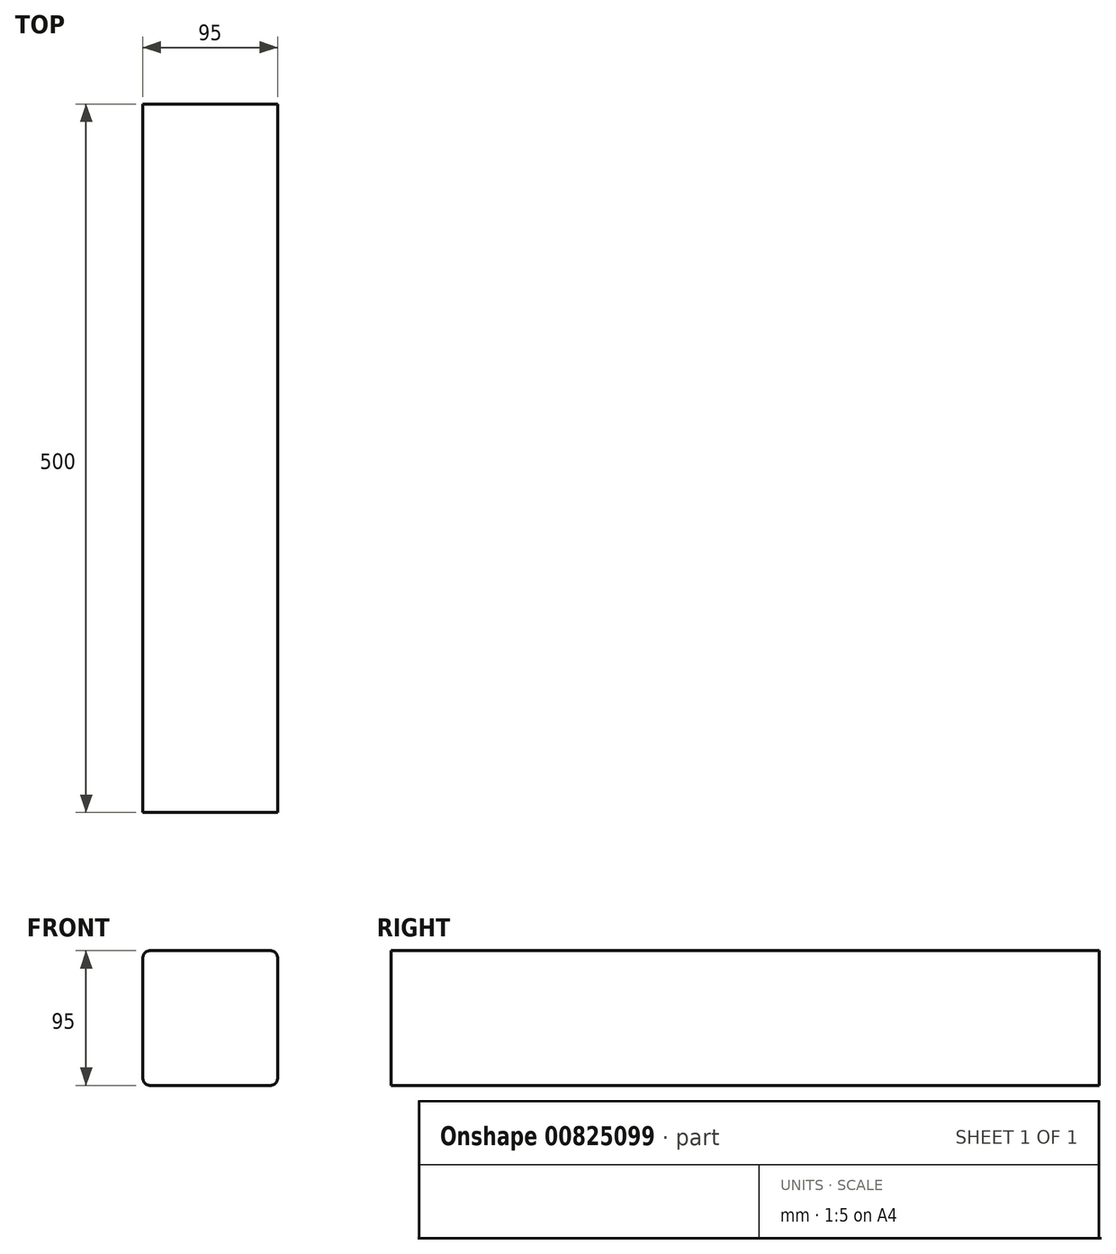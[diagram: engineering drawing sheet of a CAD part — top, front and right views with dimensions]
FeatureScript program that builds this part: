
annotation { "Feature Type Name" : "Feature", "Feature Type Description" : "" }
export const myFeature = defineFeature(function(context is Context, id is Id, definition is map)
    precondition{}
    {
        {
            var Q0;
            Q0=qCreatedBy(makeId("Front.planeOp"),FACE);
            var sketch = newSketch(context, id + "F0", { "sketchPlane" : qUnion([Q0])});
            skLineSegment(sketch, "E0.bottom", {"start": v(-40.21, 39.14) * mm, "end": v(44.79, 39.14) * mm});
            skLineSegment(sketch, "E0.top", {"start": v(-40.21, -55.86) * mm, "end": v(44.79, -55.86) * mm});
            skLineSegment(sketch, "E0.left", {"start": v(-45.21, 34.14) * mm, "end": v(-45.21, -50.86) * mm});
            skLineSegment(sketch, "E0.right", {"start": v(49.79, 34.14) * mm, "end": v(49.79, -50.86) * mm});
            skPoint(sketch, "E1.visualSharp", {"position": v(-45.21, 39.14) * mm});
            skArc(sketch, "E1.filletArc", {"start": v(-40.21, 39.14) * mm, "mid": v(-43.75, 37.67) * mm, "end": v(-45.21, 34.14) * mm});
            skPoint(sketch, "E2.visualSharp", {"position": v(49.79, 39.14) * mm});
            skArc(sketch, "E2.filletArc", {"start": v(49.79, 34.14) * mm, "mid": v(48.32, 37.67) * mm, "end": v(44.79, 39.14) * mm});
            skPoint(sketch, "E3.visualSharp", {"position": v(49.79, -55.86) * mm});
            skArc(sketch, "E3.filletArc", {"start": v(44.79, -55.86) * mm, "mid": v(48.32, -54.4) * mm, "end": v(49.79, -50.86) * mm});
            skPoint(sketch, "E4.visualSharp", {"position": v(-45.21, -55.86) * mm});
            skArc(sketch, "E4.filletArc", {"start": v(-45.21, -50.86) * mm, "mid": v(-43.75, -54.4) * mm, "end": v(-40.21, -55.86) * mm});
            skSolve(sketch);
        }
        {
            var Q0;
            Q0=makeQuery(id+"F0.imprint","IMPRINT",FACE,{"disambiguationData":[TD([[makeQuery(id+"F0.imprint","IMPRINT",EDGE,{"derivedFrom":sQuery(id+"F0.wireOp",EDGE,"E0.bottom")}),-1.0]])]});
            extrude(context, id + "F1", {"entities" : qUnion([Q0]), "depth" : 500 * mm, "offsetDistance" : 25 * mm});
        }
    });
